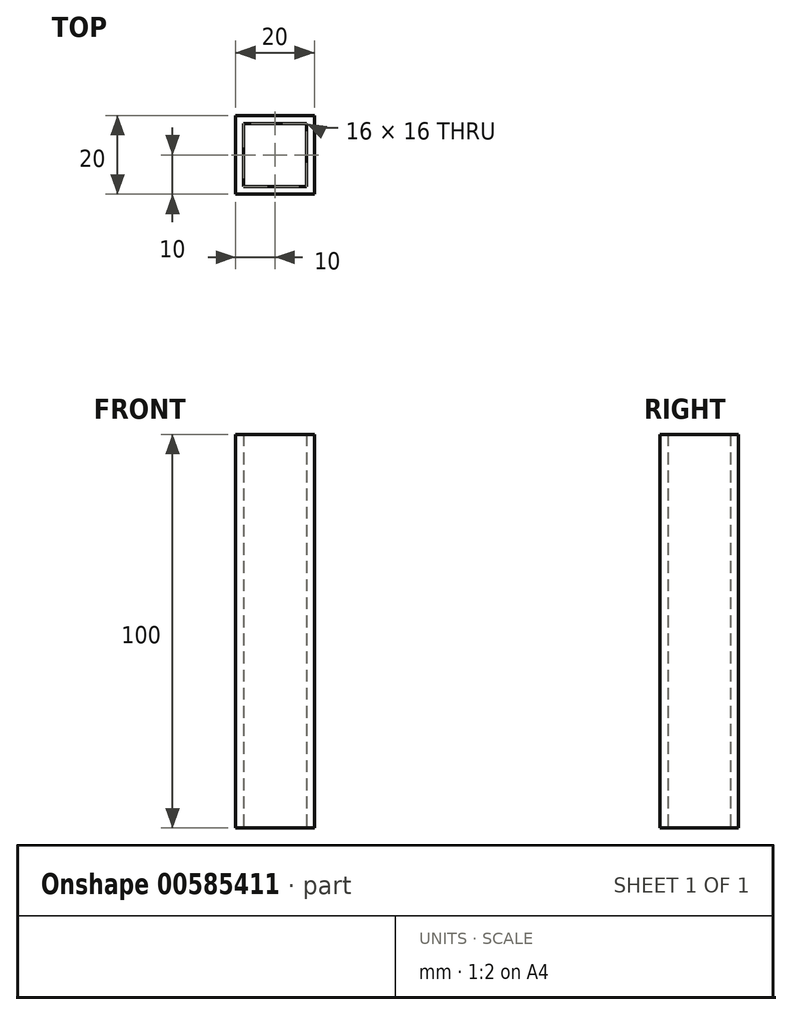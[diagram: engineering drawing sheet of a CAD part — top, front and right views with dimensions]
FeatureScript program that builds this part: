
annotation { "Feature Type Name" : "Feature", "Feature Type Description" : "" }
export const myFeature = defineFeature(function(context is Context, id is Id, definition is map)
    precondition{}
    {
        {
            var Q0;
            Q0=qCreatedBy(makeId("Top.planeOp"),FACE);
            var sketch = newSketch(context, id + "F0", { "sketchPlane" : qUnion([Q0])});
            skLineSegment(sketch, "E0.bottom", {"start": v(10, -10) * mm, "end": v(-10, -10) * mm});
            skLineSegment(sketch, "E0.top", {"start": v(10, 10) * mm, "end": v(-10, 10) * mm});
            skLineSegment(sketch, "E0.left", {"start": v(10, -10) * mm, "end": v(10, 10) * mm});
            skLineSegment(sketch, "E0.right", {"start": v(-10, -10) * mm, "end": v(-10, 10) * mm});
            skPoint(sketch, "E0.middle", {"position": v(0, 0) * mm});
            skLineSegment(sketch, "E1.0", {"start": v(8, 8) * mm, "end": v(-8, 8) * mm});
            skLineSegment(sketch, "E1.1", {"start": v(8, -8) * mm, "end": v(8, 8) * mm});
            skLineSegment(sketch, "E1.2", {"start": v(8, -8) * mm, "end": v(-8, -8) * mm});
            skLineSegment(sketch, "E1.3", {"start": v(-8, -8) * mm, "end": v(-8, 8) * mm});
            skSolve(sketch);
        }
        {
            var Q0;
            Q0=makeQuery(id+"F0.imprint","IMPRINT",FACE,{"disambiguationData":[TD([[makeQuery(id+"F0.imprint","IMPRINT",EDGE,{"derivedFrom":sQuery(id+"F0.wireOp",EDGE,"E0.bottom")}),-1.0]])]});
            extrude(context, id + "F1", {"entities" : qUnion([Q0]), "depth" : 100 * mm, "offsetDistance" : 25 * mm});
        }
    });
